# Revit family: MIA13_63_UN_Downlighter_ETK
name_source: partatom
category: Lighting Fixtures
revit_build: Autodesk Revit 2017 (Build: 20190508_0315(x64)
units: mm (PartAtom-declared; Revit-internal decimal feet)

## family parameters
Always vertical = Yes
Cut with Voids When Loaded = No
Light Source = No
OmniClass Number = 23.80.70.11.14.11
OmniClass Title = Downlights
Part Type = Normal
Room Calculation Point = Yes
Round Connector Dimension = Use Diameter
Shared = No
Work Plane-Based = No

## types (8) — shared parameters
Apparent Load = 18 VA
Assembly Code = 63.0
Bundle = 110°
Calc_Radius_glass = 113 mm
Calc_Radius_housing = 110 mm  [stored 0.360892 ft]
Diameter = 240 mm  [stored 0.787402 ft]
IfcExportAs = IfcLightFixtureType
IfcExportType = USERDEFINED
Lamp = LED
Manufacturer = ETK licht B.V.
Model = MIA.1
Radius = 120 mm  [stored 0.393701 ft]
Type Comments = IP40
URL = http://www.etk.nl
Voltage = 230 V
Wattage Comments = 18W

## per-type parameters (varying)
| type | Light Source | Luminaire_Material |
| MIA.1310.15 - Ø240 / 18W / 1800lm / 3000K | MIA.13 - Lightsource : MIA.1310.15 - Ø240 / 18W / 1800lm / 3000K | RAL9003 |
| MIA.1310.25/35 - Ø240 / 18W / 1800lm / 3000K | MIA.13 - Lightsource : MIA.1310.25/35 - Ø240 / 18W / 1800lm / 3000K | RAL9005 |
| MIA.1360.15 - Ø240 / 18W / 1980lm / 4000K | MIA.13 - Lightsource : MIA.1360.15 - Ø240 / 18W / 1980lm / 4000K | RAL9003 |
| MIA.1360.25/35 - Ø240 / 18W / 1980lm / 4000K | MIA.13 - Lightsource : MIA.1360.25/35 - Ø240 / 18W / 1980lm / 4000K | RAL9005 |
| MIA.1313.15 - Ø240 / 18W / 1800lm / 3000K | MIA.13 - Lightsource : MIA.1313.15 - Ø240 / 18W / 1800lm / 3000K | RAL9003 |
| MIA.1363.15 - Ø240 / 18W / 1980lm / 4000K | MIA.13 - Lightsource : MIA.1363.15 - Ø240 / 18W / 1980lm / 4000K | RAL9003 |
| MIA.1363.25/35 - Ø240 / 18W / 1980lm / 4000K | MIA.13 - Lightsource : MIA.1363.25/35 - Ø240 / 18W / 1980lm / 4000K | RAL9005 |
| MIA.1313.25/35 - Ø240 / 18W / 1800lm / 3000K | MIA.13 - Lightsource : MIA.1313.25/35 - Ø240 / 18W / 1800lm / 3000K | RAL9005 |

note: [stored X ft] marks values corroborated as IEEE doubles in the binary element streams (Revit-internal decimal feet)

## geometry (parser evidence)
native form markers: Sweep x3
no freeform markers — native parametric forms only
